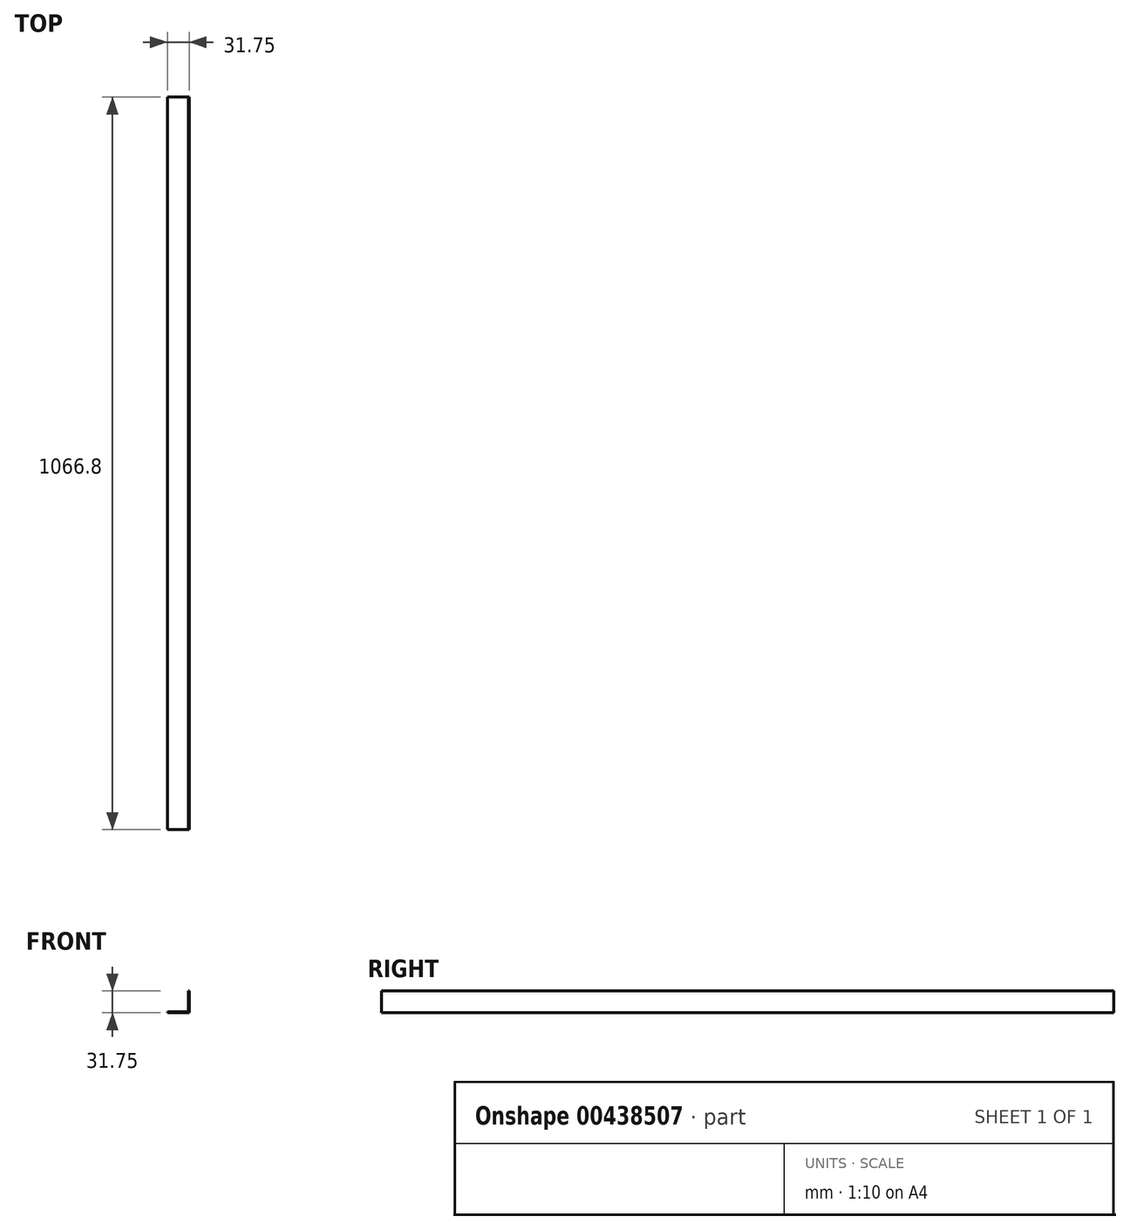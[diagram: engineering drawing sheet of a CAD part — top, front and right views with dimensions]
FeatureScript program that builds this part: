
annotation { "Feature Type Name" : "Feature", "Feature Type Description" : "" }
export const myFeature = defineFeature(function(context is Context, id is Id, definition is map)
    precondition{}
    {
        {
            var Q0;
            Q0=qCreatedBy(makeId("Front.planeOp"),FACE);
            var sketch = newSketch(context, id + "F0", { "sketchPlane" : qUnion([Q0])});
            skLineSegment(sketch, "E0", {"start": v(0, 0) * mm, "end": v(0, 31.75) * mm});
            skLineSegment(sketch, "E1", {"start": v(0, 31.75) * mm, "end": v(-1.2, 31.75) * mm});
            skLineSegment(sketch, "E2", {"start": v(-1.2, 31.75) * mm, "end": v(-1.2, 1.2) * mm});
            skLineSegment(sketch, "E3", {"start": v(-1.2, 1.2) * mm, "end": v(-31.75, 1.2) * mm});
            skLineSegment(sketch, "E4", {"start": v(-31.75, 1.2) * mm, "end": v(-31.75, 0) * mm});
            skLineSegment(sketch, "E5", {"start": v(-31.75, 0) * mm, "end": v(0, 0) * mm});
            skSolve(sketch);
        }
        {
            var Q0;
            Q0 = qSketchRegion(id + "F0", true);
            extrude(context, id + "F1", {"entities" : qUnion([Q0]), "depth" : 1066.8 * mm});
        }
    });
